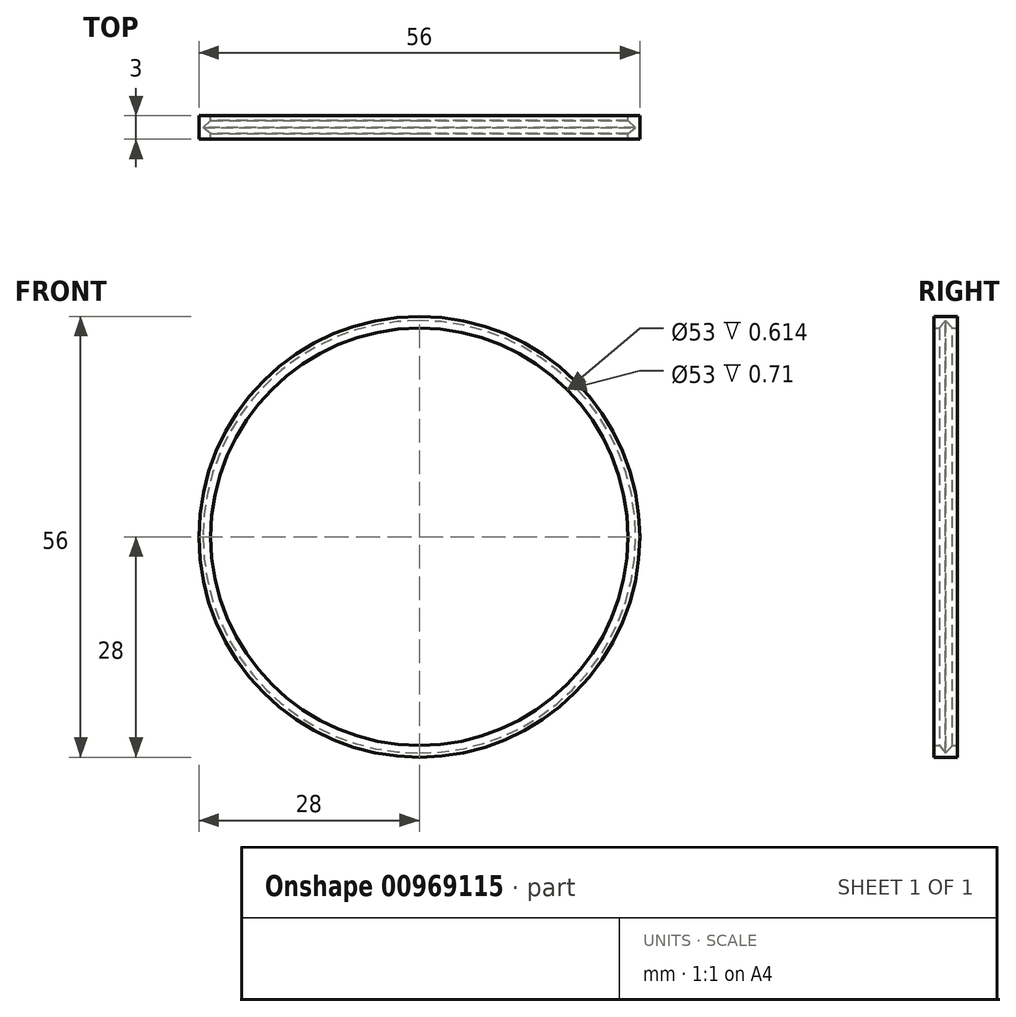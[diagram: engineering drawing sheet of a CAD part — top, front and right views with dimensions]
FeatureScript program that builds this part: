
annotation { "Feature Type Name" : "Feature", "Feature Type Description" : "" }
export const myFeature = defineFeature(function(context is Context, id is Id, definition is map)
    precondition{}
    {
        {
            var Q0;
            Q0=qCreatedBy(makeId("Front.planeOp"),FACE);
            var sketch = newSketch(context, id + "F0", { "sketchPlane" : qUnion([Q0])});
            skCircle(sketch, "E0", {"center": v(0, 0) * mm, "radius": 28 * mm});
            skCircle(sketch, "E1", {"center": v(0, 0) * mm, "radius": 26.5 * mm});
            skCircle(sketch, "E2", {"center": v(0, 0) * mm, "radius": 27.16 * mm});
            skSolve(sketch);
        }
        {
            var Q0;
            Q0=makeQuery(id+"F0.imprint","IMPRINT",FACE,{"disambiguationData":[TD([[makeQuery(id+"F0.imprint","IMPRINT",EDGE,{"derivedFrom":sQuery(id+"F0.wireOp",EDGE,"E0")}),1.0]])]});
            var Q1;
            Q1=makeQuery(id+"F0.imprint","IMPRINT",FACE,{"disambiguationData":[TD([[makeQuery(id+"F0.imprint","IMPRINT",EDGE,{"derivedFrom":sQuery(id+"F0.wireOp",EDGE,"E1")}),-1.0]])]});
            extrude(context, id + "F1", {"entities" : qUnion([Q0, Q1]), "endBound" : BoundingType.SYMMETRIC, "depth" : 3 * mm, "offsetDistance" : 25 * mm});
        }
        {
            var Q0;
            Q0=qCreatedBy(makeId("Top.planeOp"),FACE);
            var sketch = newSketch(context, id + "F2", { "sketchPlane" : qUnion([Q0])});
            skLineSegment(sketch, "E3", {"start": v(-27.48, 0) * mm, "end": v(-26.49, 0.9) * mm});
            skLineSegment(sketch, "E4", {"start": v(-26.49, 0.9) * mm, "end": v(-26.49, -0.8) * mm});
            skLineSegment(sketch, "E5", {"start": v(-26.49, -0.8) * mm, "end": v(-27.48, 0) * mm});
            skSolve(sketch);
        }
        {
            var Q0;
            Q0 = qSketchRegion(id + "F2", true);
            var Q1;
            Q1=sQuery(id+"F0.wireOp",EDGE,"E2");
            sweep(context, id + "F3", {"operationType" : NewBodyOperationType.REMOVE, "profiles" : qUnion([Q0]), "path" : qUnion([Q1])});
        }
    });
